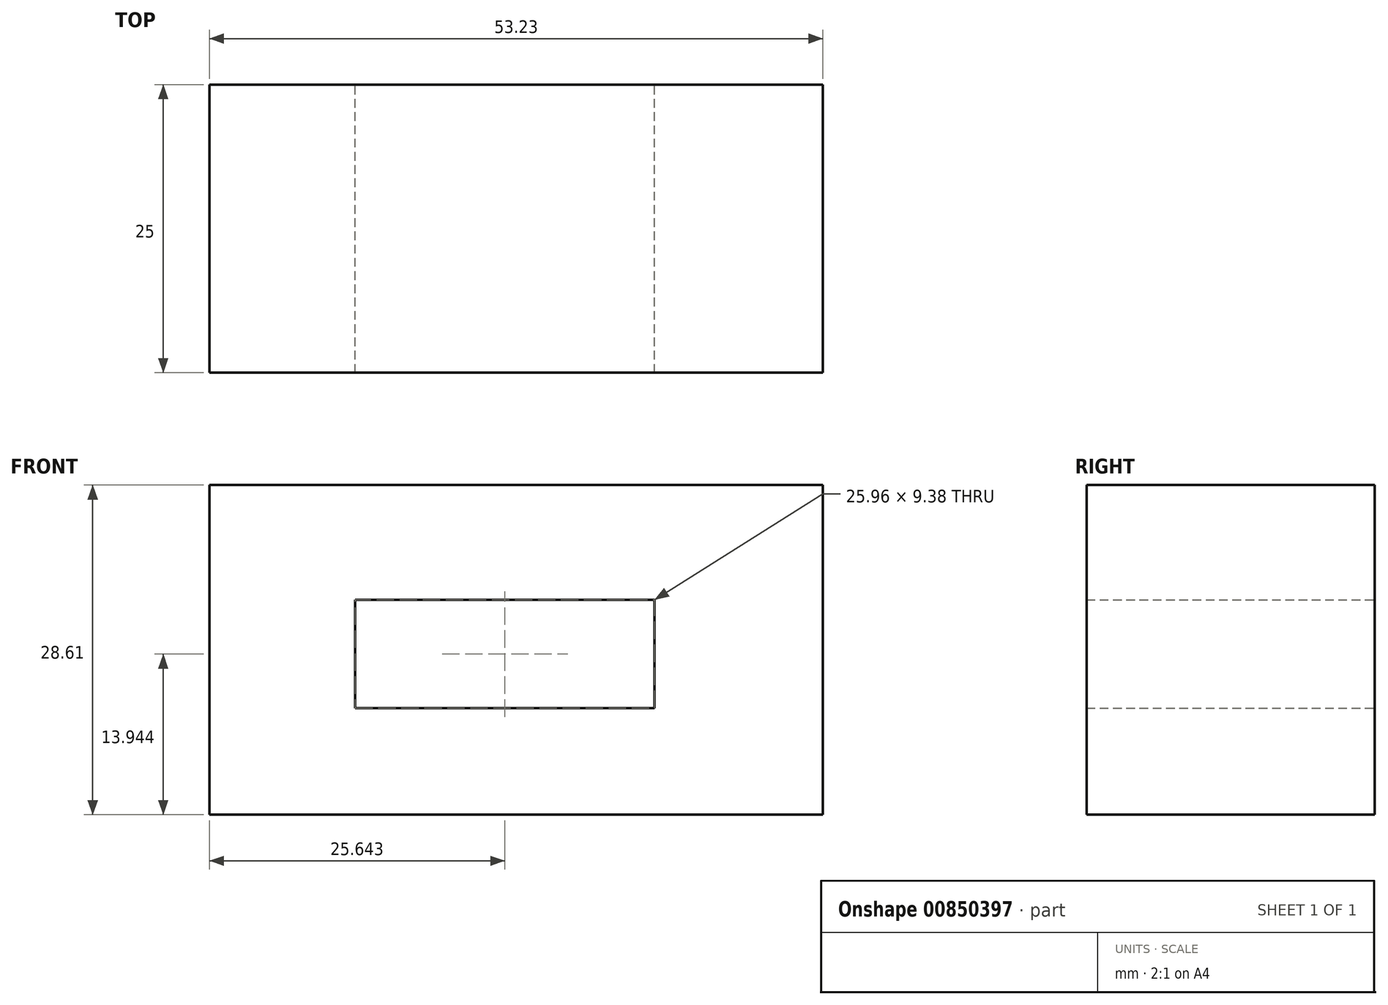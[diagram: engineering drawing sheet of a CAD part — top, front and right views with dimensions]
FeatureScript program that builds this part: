
annotation { "Feature Type Name" : "Feature", "Feature Type Description" : "" }
export const myFeature = defineFeature(function(context is Context, id is Id, definition is map)
    precondition{}
    {
        {
            var Q0;
            Q0=qCreatedBy(makeId("Front.planeOp"),FACE);
            var sketch = newSketch(context, id + "F0", { "sketchPlane" : qUnion([Q0])});
            skLineSegment(sketch, "E0.bottom", {"start": v(0, 0) * mm, "end": v(-53.23, 0) * mm});
            skLineSegment(sketch, "E0.top", {"start": v(0, 28.61) * mm, "end": v(-53.23, 28.61) * mm});
            skLineSegment(sketch, "E0.left", {"start": v(0, 0) * mm, "end": v(0, 28.61) * mm});
            skLineSegment(sketch, "E0.right", {"start": v(-53.23, 0) * mm, "end": v(-53.23, 28.61) * mm});
            skLineSegment(sketch, "E1.bottom", {"start": v(-40.57, 18.63) * mm, "end": v(-14.6, 18.63) * mm});
            skLineSegment(sketch, "E1.top", {"start": v(-40.57, 9.25) * mm, "end": v(-14.6, 9.25) * mm});
            skLineSegment(sketch, "E1.left", {"start": v(-40.57, 18.63) * mm, "end": v(-40.57, 9.25) * mm});
            skLineSegment(sketch, "E1.right", {"start": v(-14.6, 18.63) * mm, "end": v(-14.6, 9.25) * mm});
            skSolve(sketch);
        }
        {
            var Q0;
            Q0 = qSketchRegion(id + "F0", true);
            extrude(context, id + "F1", {"entities" : qUnion([Q0]), "depth" : 25 * mm, "offsetDistance" : 25 * mm});
        }
    });
